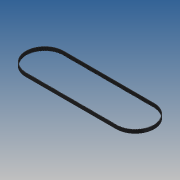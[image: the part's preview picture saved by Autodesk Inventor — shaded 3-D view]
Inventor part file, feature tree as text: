
AUTODESK INVENTOR PART (.ipt)
format: ipt  version: 2013 (Build 170138000, 138)  size: 636,416 bytes
history: native  units: mm
features: sketch x5, extrude x4, pattern_linear x1
ambient origin geometry x8: Origin, YZ Plane, XZ Plane, XY Plane, X Axis, Y Axis, Z Axis, Center Point
bodies: Solid1 (feature_tree)
feature tree (10):
  extrude  "Extrusion1"  Depth=31.830989mm
  extrude  "Extrusion2"  TaperAngle=180.0deg  [1 undecoded]
  extrude  "Extrusion4"  Depth=0.375mm
  sketch  "Sketch8"  dims[d15=6.0mm d16=0.0mm d17=6.0mm d18=0.0mm d19=2500.0mm]
  extrude  "Extrusion5"  Depth=0.629mm
  pattern_linear  "Rectangular Pattern1"  Spacing1=6.0mm  [1 undecoded]
  sketch  "Sketch1"  dims[d0=31.830989mm d2=31.830989mm]
  sketch  "Sketch2"  dims[d3=151.5mm d4=180.0deg]
  sketch  "Sketch5"  dims[d5=6.0mm d6=0.0mm d7=0.375mm]
  sketch  "Sketch7"  dims[d8=6.0mm d9=0.0mm d14=0.629mm]
note: 2 required parameter values undecoded (feature->parameter linkage not recoverable at this tier; creation-order binding heuristic only, values carry confidence <= 0.55)
